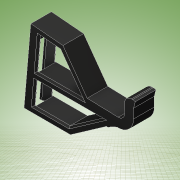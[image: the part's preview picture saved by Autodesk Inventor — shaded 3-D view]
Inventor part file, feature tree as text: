
AUTODESK INVENTOR PART (.ipt)
format: ipt  version: 2017 (Build 210142000, 142)  size: 211,968 bytes
history: native  units: in
note: dims shown in document units (in); Inventor stores cm internally (conversion verified against a paired STEP export)
features: extrude x2, sketch x2, plane x1, chamfer x1
ambient origin geometry x8: Origin, YZ Plane, XZ Plane, XY Plane, X Axis, Y Axis, Z Axis, Center Point
bodies: Solid1 (feature_tree)
feature tree (6):
  extrude  "Extrusion1"  Depth=0.2in
  plane  "Work Plane1"
  extrude  "Extrusion2"  Depth=0.25in TaperAngle=0.0deg
  chamfer  "Chamfer3"  Distance=1.5in
  sketch  "Sketch1"  dims[d3=0.2in d6=0.0344in]
  sketch  "Sketch2"  dims[d7=0.6in d8=0.0in d24=1.0in d25=0.0in d27=0.5in d28=0.2165in d29=0.2165in d30=0.0787in d31=0.0787in d32=0.0079in d33=1.0651in d34=1.0651in d36=0.9in d37=1.5in d39=2.38in d40=0.754in d41=0.446in d42=0.2715in d43=0.1849in d44=0.2715in d45=0.1825in d46=0.2in d47=180.0deg d48=90.0deg d51=0.25in d52=1.0in d53=0.0in d54=0.015in d55=0.175in d56=0.175in d57=0.175in d58=0.175in d59=0.25in d60=0.25in d67=0.3in d68=0.05in d69=0.125in d70=45.0deg]
